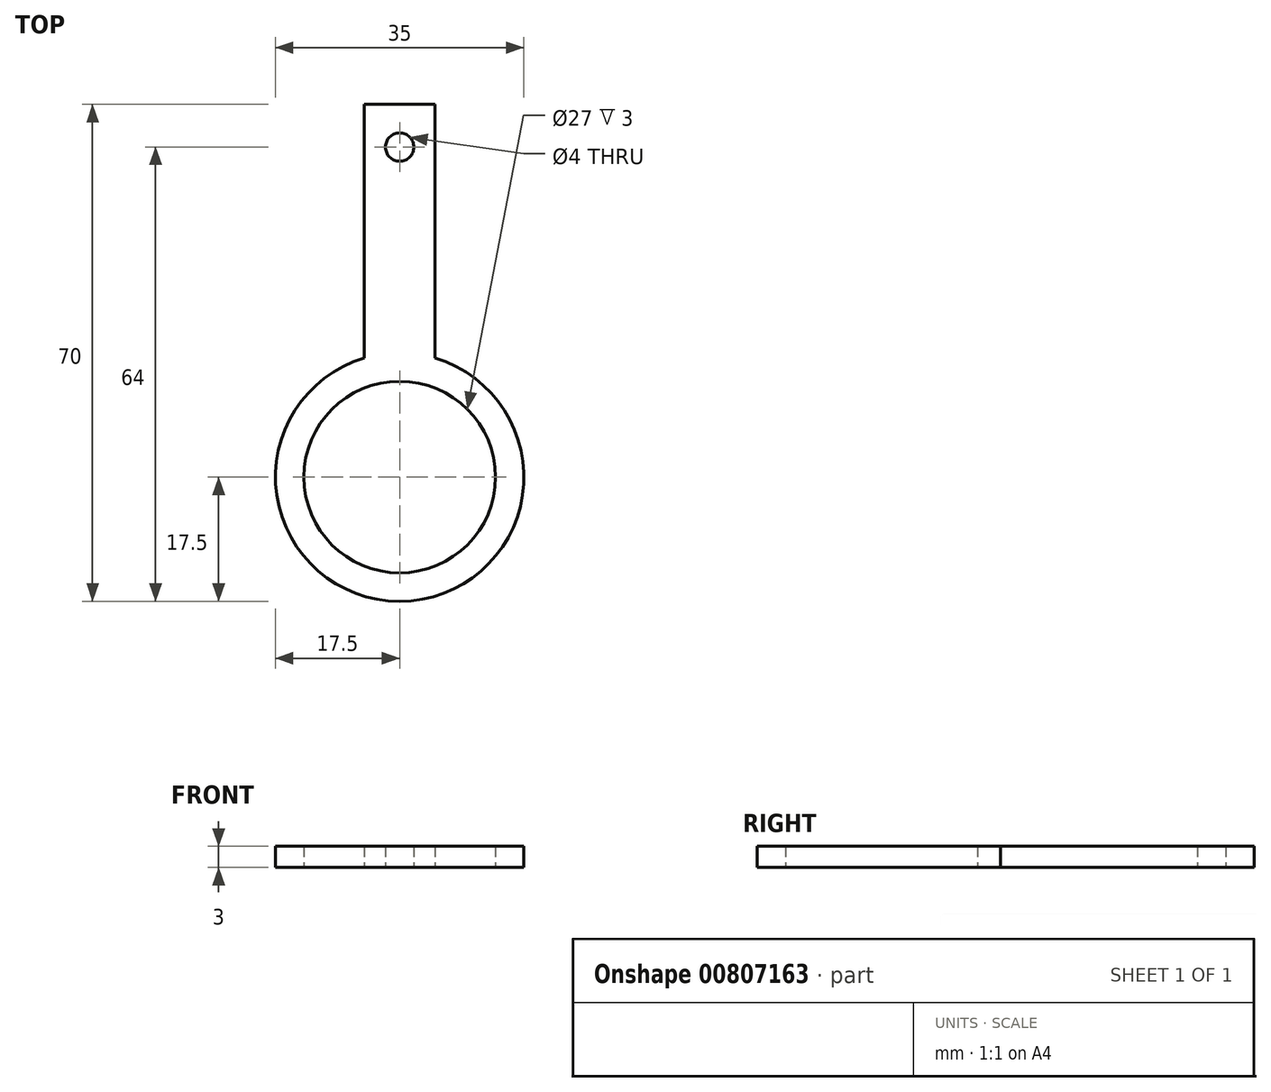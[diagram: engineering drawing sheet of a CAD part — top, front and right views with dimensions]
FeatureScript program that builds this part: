
annotation { "Feature Type Name" : "Feature", "Feature Type Description" : "" }
export const myFeature = defineFeature(function(context is Context, id is Id, definition is map)
    precondition{}
    {
        {
            var Q0;
            Q0=qCreatedBy(makeId("Top.planeOp"),FACE);
            var sketch = newSketch(context, id + "F0", { "sketchPlane" : qUnion([Q0])});
            skCircle(sketch, "E0", {"center": v(0, 0) * mm, "radius": 17.5 * mm});
            skCircle(sketch, "E1", {"center": v(0, 0) * mm, "radius": 13.5 * mm});
            skLineSegment(sketch, "E2.bottom", {"start": v(5, 52.5) * mm, "end": v(-5, 52.5) * mm});
            skLineSegment(sketch, "E2.left", {"start": v(5, 52.5) * mm, "end": v(5, 17.5) * mm});
            skLineSegment(sketch, "E2.right", {"start": v(-5, 52.5) * mm, "end": v(-5, 17.5) * mm});
            skPoint(sketch, "E2.middle", {"position": v(0, 35) * mm});
            skCircle(sketch, "E3", {"center": v(0, 46.5) * mm, "radius": 2 * mm});
            skLineSegment(sketch, "E4.left", {"start": v(-5, 17.5) * mm, "end": v(-5, 15.2) * mm});
            skLineSegment(sketch, "E4.right", {"start": v(5, 17.5) * mm, "end": v(5, 15.2) * mm});
            skSolve(sketch);
        }
        {
            var Q0;
            Q0=makeQuery(id+"F0.imprint","IMPRINT",FACE,{"disambiguationData":[TD([[makeQuery(id+"F0.imprint","IMPRINT",EDGE,{"derivedFrom":sQuery(id+"F0.wireOp",EDGE,"E0")}),1.0]])]});
            var Q1;
            Q1=makeQuery(id+"F0.imprint","IMPRINT",FACE,{"disambiguationData":[TD([[makeQuery(id+"F0.imprint","IMPRINT",EDGE,{"derivedFrom":sQuery(id+"F0.wireOp",EDGE,"E2.bottom")}),1.0]])]});
            extrude(context, id + "F1", {"entities" : qUnion([Q0, Q1]), "depth" : 3 * mm, "offsetDistance" : 25 * mm});
        }
    });
